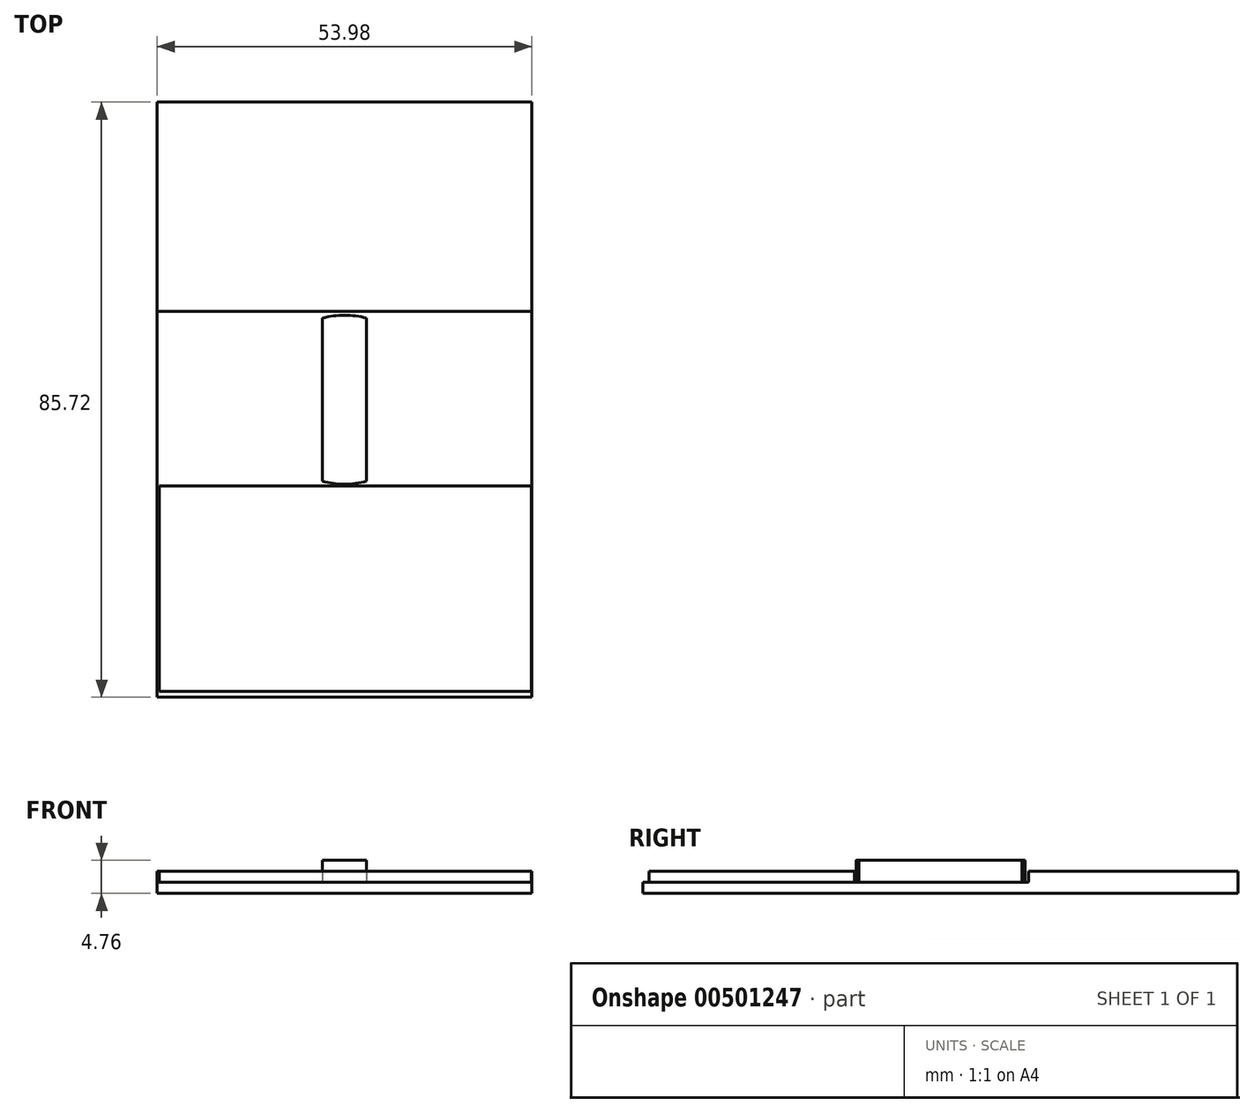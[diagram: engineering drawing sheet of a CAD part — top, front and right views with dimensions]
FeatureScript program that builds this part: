
annotation { "Feature Type Name" : "Feature", "Feature Type Description" : "" }
export const myFeature = defineFeature(function(context is Context, id is Id, definition is map)
    precondition{}
    {
        {
            var Q0;
            Q0=qCreatedBy(makeId("Top.planeOp"),FACE);
            var sketch = newSketch(context, id + "F0", { "sketchPlane" : qUnion([Q0])});
            skLineSegment(sketch, "E0.bottom", {"start": v(26.99, -42.86) * mm, "end": v(-26.99, -42.86) * mm});
            skLineSegment(sketch, "E0.top", {"start": v(26.99, 42.86) * mm, "end": v(-26.99, 42.86) * mm});
            skLineSegment(sketch, "E0.left", {"start": v(26.99, -42.86) * mm, "end": v(26.99, 42.86) * mm});
            skLineSegment(sketch, "E0.right", {"start": v(-26.99, -42.86) * mm, "end": v(-26.99, 42.86) * mm});
            skPoint(sketch, "E0.middle", {"position": v(0, 0) * mm});
            skSolve(sketch);
        }
        {
            var Q0;
            Q0 = qSketchRegion(id + "F0", true);
            extrude(context, id + "F1", {"entities" : qUnion([Q0]), "depth" : 1.59 * mm});
        }
        {
            var Q0;
            Q0=makeQuery(id+"F1.opExtrude","CAP_FACE",FACE,{"disambiguationData":[OSD([sQuery(id+"F0.wireOp",EDGE,"E0.bottom"),sQuery(id+"F0.wireOp",EDGE,"E0.top"),sQuery(id+"F0.wireOp",EDGE,"E0.left"),sQuery(id+"F0.wireOp",EDGE,"E0.right")])],"isStart":false});
            var sketch = newSketch(context, id + "F2", { "sketchPlane" : qUnion([Q0])});
            skLineSegment(sketch, "E1.bottom", {"start": v(26.99, -12.7) * mm, "end": v(-26.99, -12.7) * mm});
            skLineSegment(sketch, "E1.top", {"start": v(26.99, 12.7) * mm, "end": v(-26.99, 12.7) * mm});
            skLineSegment(sketch, "E1.left", {"start": v(26.99, -12.7) * mm, "end": v(26.99, 12.7) * mm});
            skLineSegment(sketch, "E1.right", {"start": v(-26.99, -12.7) * mm, "end": v(-26.99, 12.7) * mm});
            skPoint(sketch, "E1.middle", {"position": v(0, 0) * mm});
            skSolve(sketch);
        }
        {
            var Q0;
            {var subQ0=sQuery(id+"F2.wireOp",EDGE,"E1.top");Q0=makeQuery(id+"F2.imprint","IMPRINT",FACE,{"disambiguationData":[TD([[makeQuery(id+"F2.imprint","IMPRINT",EDGE,{"derivedFrom":subQ0}),-1.0]])]});}
            var sketch = newSketch(context, id + "F3", { "sketchPlane" : qUnion([Q0])});
            skLineSegment(sketch, "E2.bottom", {"start": v(-26.66, 42.52) * mm, "end": v(26.54, 42.52) * mm});
            skLineSegment(sketch, "E2.top", {"start": v(-26.66, 13.14) * mm, "end": v(26.54, 13.14) * mm});
            skLineSegment(sketch, "E2.left", {"start": v(-26.66, 42.52) * mm, "end": v(-26.66, 13.14) * mm});
            skLineSegment(sketch, "E2.right", {"start": v(26.54, 42.52) * mm, "end": v(26.54, 13.14) * mm});
            skLineSegment(sketch, "E3.bottom", {"start": v(-26.68, -12.41) * mm, "end": v(26.91, -12.41) * mm});
            skLineSegment(sketch, "E3.top", {"start": v(-26.68, -41.98) * mm, "end": v(26.91, -41.98) * mm});
            skLineSegment(sketch, "E3.left", {"start": v(-26.68, -12.41) * mm, "end": v(-26.68, -41.98) * mm});
            skLineSegment(sketch, "E3.right", {"start": v(26.91, -12.41) * mm, "end": v(26.91, -41.98) * mm});
            skSolve(sketch);
        }
        {
            var Q0;
            Q0=makeQuery(id+"F3.imprint","IMPRINT",FACE,{"disambiguationData":[TD([[makeQuery(id+"F3.imprint","IMPRINT",EDGE,{"derivedFrom":sQuery(id+"F3.wireOp",EDGE,"E3.bottom")}),-1.0]])]});
            extrude(context, id + "F4", {"entities" : qUnion([Q0]), "operationType" : NewBodyOperationType.ADD, "depth" : 1.59 * mm});
        }
        {
            var Q0;
            {var subQ0=sQuery(id+"F2.wireOp",EDGE,"E1.top");Q0=makeQuery(id+"F2.imprint","IMPRINT",FACE,{"disambiguationData":[TD([[makeQuery(id+"F2.imprint","IMPRINT",EDGE,{"derivedFrom":subQ0}),-1.0]])]});}
            extrude(context, id + "F5", {"entities" : qUnion([Q0]), "operationType" : NewBodyOperationType.ADD, "depth" : 1.59 * mm});
        }
        {
            var Q0;
            Q0=makeQuery(id+"F1.opExtrude","CAP_FACE",FACE,{"disambiguationData":[OSD([sQuery(id+"F0.wireOp",EDGE,"E0.bottom"),sQuery(id+"F0.wireOp",EDGE,"E0.top"),sQuery(id+"F0.wireOp",EDGE,"E0.left"),sQuery(id+"F0.wireOp",EDGE,"E0.right")])],"isStart":false});
            var sketch = newSketch(context, id + "F6", { "sketchPlane" : qUnion([Q0])});
            skCircle(sketch, "E4", {"center": v(0, 0) * mm, "radius": 12.41 * mm});
            skSolve(sketch);
        }
        {
            var Q0;
            Q0=sQuery(id+"F6.wireOp",EDGE,"E4");
            extrude(context, id + "F7", {"bodyType" : ToolBodyType.SURFACE, "surfaceEntities" : qUnion([Q0]), "depth" : 2.2 * mm});
        }
        {
            var Q0;
            Q0=makeQuery(id+"F1.opExtrude","CAP_FACE",FACE,{"disambiguationData":[OSD([sQuery(id+"F0.wireOp",EDGE,"E0.bottom"),sQuery(id+"F0.wireOp",EDGE,"E0.top"),sQuery(id+"F0.wireOp",EDGE,"E0.left"),sQuery(id+"F0.wireOp",EDGE,"E0.right")])],"isStart":false});
            var sketch = newSketch(context, id + "F8", { "sketchPlane" : qUnion([Q0])});
            skLineSegment(sketch, "E5.left", {"start": v(3.18, -11.74) * mm, "end": v(3.18, 11.74) * mm});
            skLineSegment(sketch, "E5.right", {"start": v(-3.18, -11.74) * mm, "end": v(-3.18, 11.74) * mm});
            skPoint(sketch, "E5.middle", {"position": v(0, 0) * mm});
            skArc(sketch, "E6", {"start": v(3.17, 11.74) * mm, "mid": v(0, 12.17) * mm, "end": v(-3.17, 11.74) * mm});
            skArc(sketch, "E7.trimOffspring", {"start": v(-3.18, -11.74) * mm, "mid": v(0, -12.17) * mm, "end": v(3.17, -11.74) * mm});
            skPoint(sketch, "E8.orphan", {"position": v(3.18, 12.41) * mm});
            skPoint(sketch, "E9.orphan", {"position": v(-3.18, 12.41) * mm});
            skPoint(sketch, "E10.orphan", {"position": v(3.18, -12.41) * mm});
            skPoint(sketch, "E11.orphan", {"position": v(-3.18, -12.41) * mm});
            skSolve(sketch);
        }
        {
            var Q0;
            Q0 = qSketchRegion(id + "F8", true);
            var Q1;
            Q1=makeQuery(id+"F8.imprint","IMPRINT",FACE,{"disambiguationData":[TD([[makeQuery(id+"F8.imprint","IMPRINT",EDGE,{"derivedFrom":sQuery(id+"F8.wireOp",EDGE,"E5.left")}),1.0]])]});
            extrude(context, id + "F9", {"entities" : qUnion([Q0, Q1]), "operationType" : NewBodyOperationType.ADD, "depth" : 1.59 * mm});
        }
        {
            var Q0;
            Q0=makeQuery(id+"F9.opExtrude","CAP_FACE",FACE,{"disambiguationData":[OSD([sQuery(id+"F8.wireOp",EDGE,"E5.left"),sQuery(id+"F8.wireOp",EDGE,"E5.right"),sQuery(id+"F8.wireOp",EDGE,"E6"),sQuery(id+"F8.wireOp",EDGE,"E7.trimOffspring")])],"isStart":false});
            extrude(context, id + "F10", {"entities" : qUnion([Q0]), "operationType" : NewBodyOperationType.ADD, "depth" : 1.59 * mm});
        }
    });
